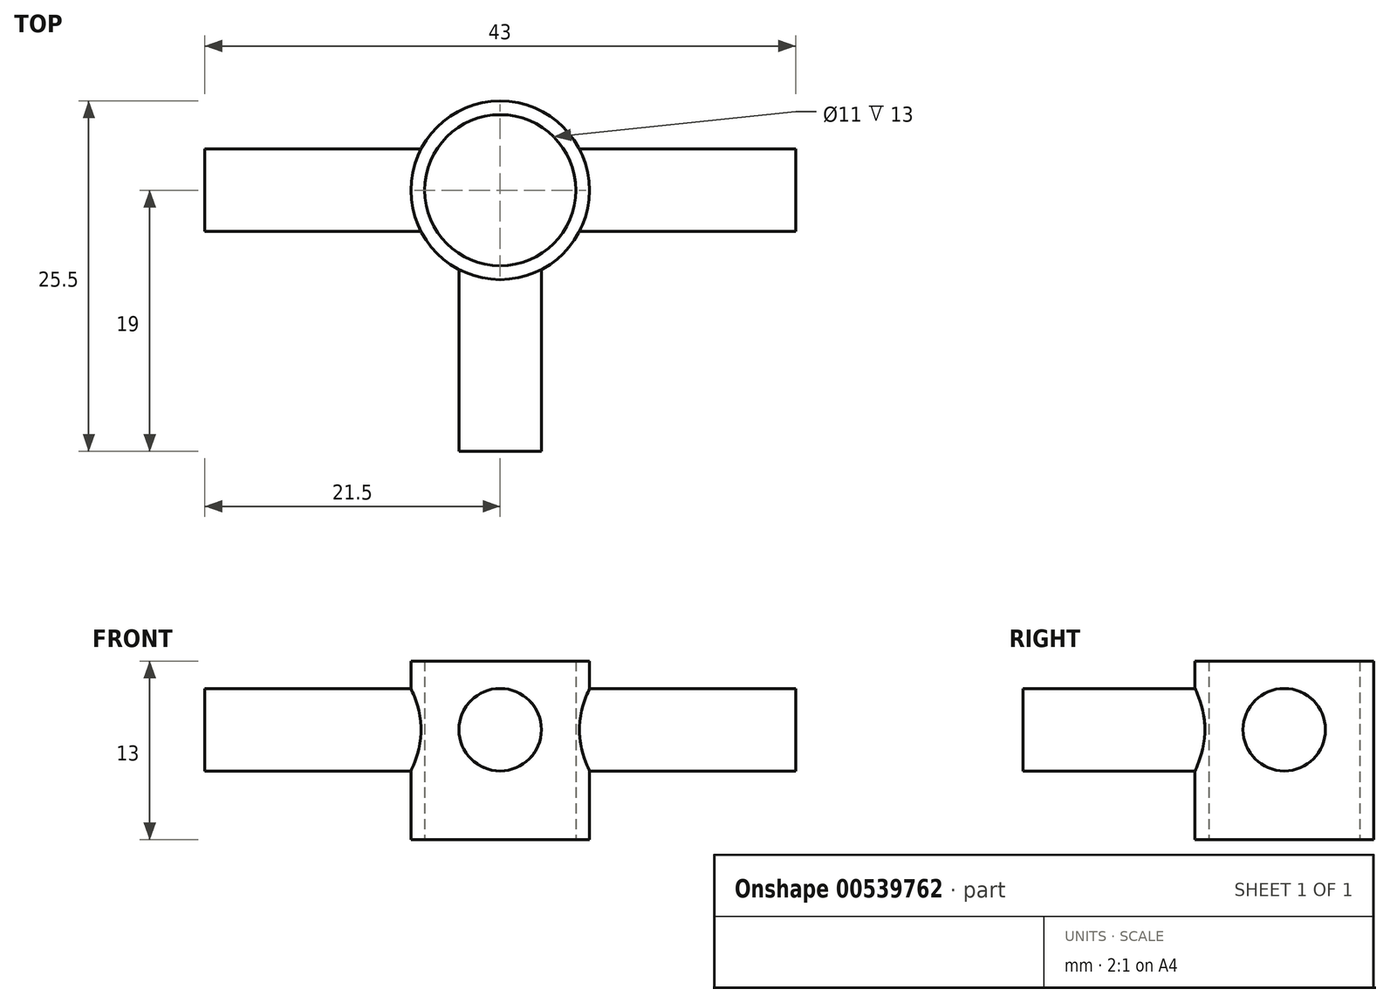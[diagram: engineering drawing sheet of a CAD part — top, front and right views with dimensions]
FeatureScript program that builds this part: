
annotation { "Feature Type Name" : "Feature", "Feature Type Description" : "" }
export const myFeature = defineFeature(function(context is Context, id is Id, definition is map)
    precondition{}
    {
        {
            var Q0;
            Q0=qCreatedBy(makeId("Top.planeOp"),FACE);
            var sketch = newSketch(context, id + "F0", { "sketchPlane" : qUnion([Q0])});
            skCircle(sketch, "E0", {"center": v(0, 0) * mm, "radius": 6.5 * mm});
            skSolve(sketch);
        }
        {
            var Q0;
            Q0=makeQuery(id+"F0.imprint","IMPRINT",FACE,{"disambiguationData":[TD([[makeQuery(id+"F0.imprint","IMPRINT",EDGE,{"derivedFrom":sQuery(id+"F0.wireOp",EDGE,"E0")}),1.0]])]});
            extrude(context, id + "F1", {"entities" : qUnion([Q0]), "depth" : 13 * mm, "offsetDistance" : 25 * mm});
        }
        {
            var Q0;
            Q0=qCreatedBy(makeId("Right.planeOp"),FACE);
            var sketch = newSketch(context, id + "F2", { "sketchPlane" : qUnion([Q0])});
            skCircle(sketch, "E1", {"center": v(0, 8) * mm, "radius": 3 * mm});
            skSolve(sketch);
        }
        {
            var Q0;
            Q0 = qSketchRegion(id + "F2", true);
            extrude(context, id + "F3", {"entities" : qUnion([Q0]), "operationType" : NewBodyOperationType.ADD, "depth" : 43 * mm, "offsetDistance" : 25 * mm, "symmetric" : true});
        }
        {
            var Q0;
            Q0=qCreatedBy(makeId("Front.planeOp"),FACE);
            var sketch = newSketch(context, id + "F4", { "sketchPlane" : qUnion([Q0])});
            skCircle(sketch, "E2", {"center": v(0, 8) * mm, "radius": 3 * mm});
            skSolve(sketch);
        }
        {
            var Q0;
            Q0 = qSketchRegion(id + "F4", true);
            extrude(context, id + "F5", {"entities" : qUnion([Q0]), "operationType" : NewBodyOperationType.ADD, "depth" : 19 * mm, "offsetDistance" : 25 * mm, "hasDraft" : true, "draftAngle" : 0 * degree});
        }
        {
            var Q0;
            Q0=makeQuery(id+"F1.opExtrude","CAP_FACE",FACE,{"disambiguationData":[OSD([sQuery(id+"F0.wireOp",EDGE,"E0")])],"isStart":true});
            var sketch = newSketch(context, id + "F6", { "sketchPlane" : qUnion([Q0])});
            skPoint(sketch, "E3", {"position": v(0, 0) * mm});
            skSolve(sketch);
        }
        {
            var Q0;
            Q0=sQuery(id+"F6.wireOp",VERTEX,"E3");
            var Q1;
            Q1=makeQuery(id+"F1.opExtrude","SWEPT_BODY",BODY,{"disambiguationData":[OSD([sQuery(id+"F0.wireOp",EDGE,"E0")])]});
            hole(context, id + "F7", {"style" : HoleStyle.SIMPLE, "endStyle" : HoleEndStyle.THROUGH, "holeDiameter" : 11 * mm, "isTappedThrough" : true, "tappedDepth" : 12 * mm, "tapClearance" : 3, "locations" : qUnion([Q0]), "scope" : qUnion([Q1])});
        }
    });
